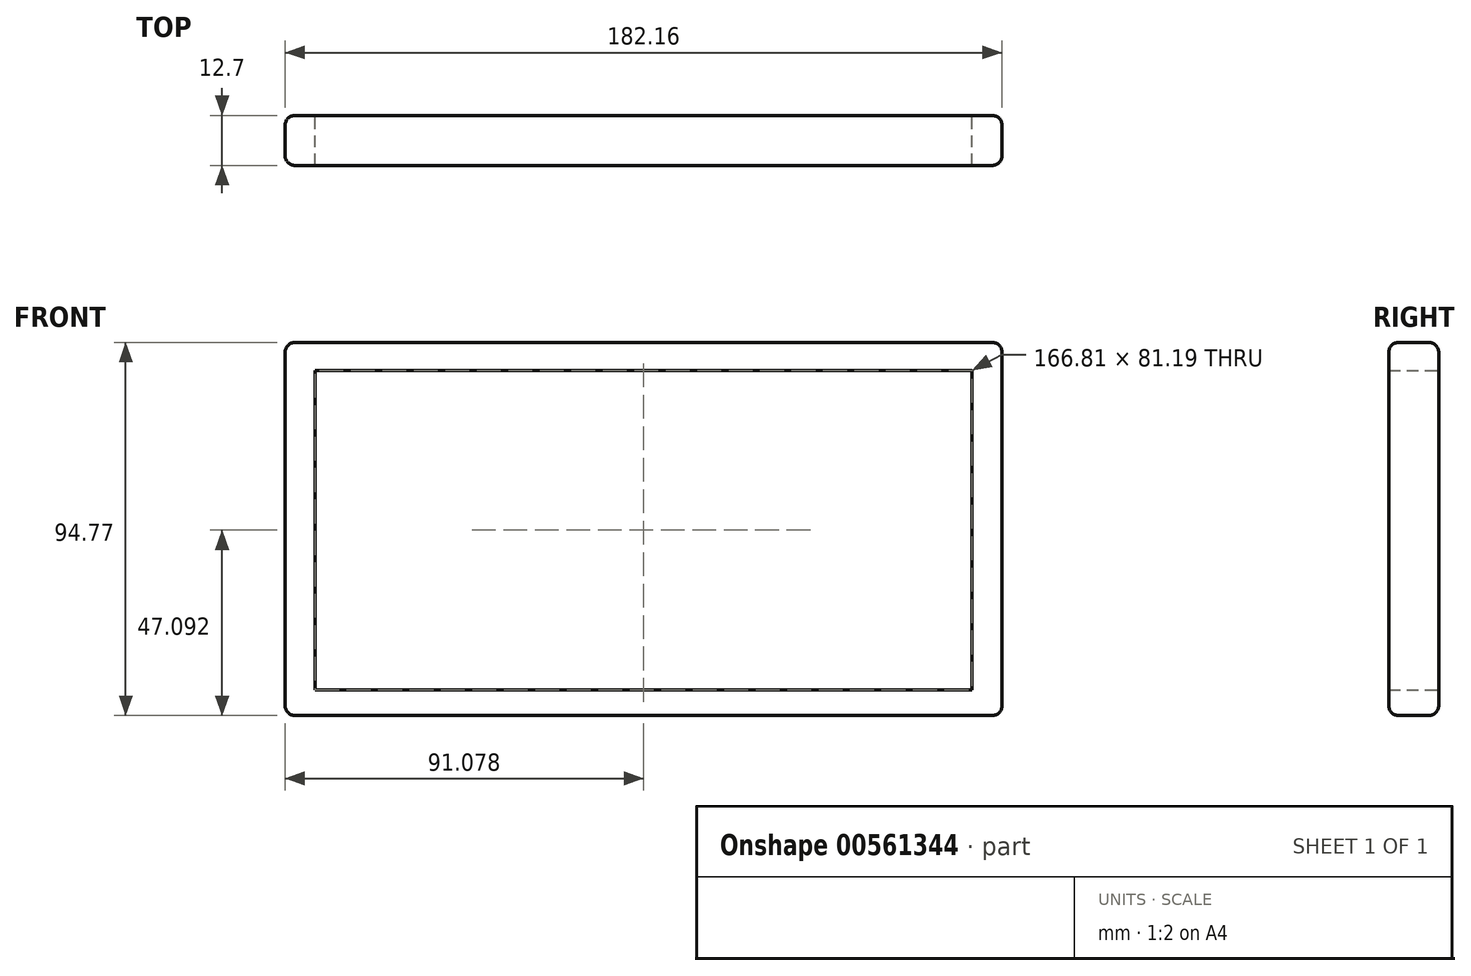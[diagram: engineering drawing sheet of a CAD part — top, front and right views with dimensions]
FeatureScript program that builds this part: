
annotation { "Feature Type Name" : "Feature", "Feature Type Description" : "" }
export const myFeature = defineFeature(function(context is Context, id is Id, definition is map)
    precondition{}
    {
        {
            var Q0;
            Q0=qCreatedBy(makeId("Front.planeOp"),FACE);
            var sketch = newSketch(context, id + "F0", { "sketchPlane" : qUnion([Q0])});
            skLineSegment(sketch, "E0.bottom", {"start": v(-92.1, 46.94) * mm, "end": v(90.07, 46.94) * mm});
            skLineSegment(sketch, "E0.top", {"start": v(-92.1, -47.83) * mm, "end": v(90.07, -47.83) * mm});
            skLineSegment(sketch, "E0.left", {"start": v(-92.1, 46.94) * mm, "end": v(-92.1, -47.83) * mm});
            skLineSegment(sketch, "E0.right", {"start": v(90.07, 46.94) * mm, "end": v(90.07, -47.83) * mm});
            skLineSegment(sketch, "E1.bottom", {"start": v(-84.42, 39.86) * mm, "end": v(82.4, 39.86) * mm});
            skLineSegment(sketch, "E1.top", {"start": v(-84.42, -41.33) * mm, "end": v(82.4, -41.33) * mm});
            skLineSegment(sketch, "E1.left", {"start": v(-84.42, 39.86) * mm, "end": v(-84.42, -41.33) * mm});
            skLineSegment(sketch, "E1.right", {"start": v(82.4, 39.86) * mm, "end": v(82.4, -41.33) * mm});
            skSolve(sketch);
        }
        {
            var Q0;
            Q0=makeQuery(id+"F0.imprint","IMPRINT",FACE,{"disambiguationData":[TD([[makeQuery(id+"F0.imprint","IMPRINT",EDGE,{"derivedFrom":sQuery(id+"F0.wireOp",EDGE,"E0.bottom")}),-1.0]])]});
            extrude(context, id + "F1", {"entities" : qUnion([Q0]), "depth" : 12.7 * mm, "offsetDistance" : 25.4 * mm});
        }
        {
            var Q0;
            Q0=makeQuery(id+"F1.opExtrude","CAP_EDGE",EDGE,{"disambiguationData":[OSD([sQuery(id+"F0.wireOp",EDGE,"E0.left")])],"isStart":false});
            var Q1;
            Q1=makeQuery(id+"F1.opExtrude","CAP_EDGE",EDGE,{"disambiguationData":[OSD([sQuery(id+"F0.wireOp",EDGE,"E0.bottom")])],"isStart":false});
            var Q2;
            Q2=makeQuery(id+"F1.opExtrude","CAP_EDGE",EDGE,{"disambiguationData":[OSD([sQuery(id+"F0.wireOp",EDGE,"E0.top")])],"isStart":false});
            var Q3;
            Q3=makeQuery(id+"F1.opExtrude","CAP_EDGE",EDGE,{"disambiguationData":[OSD([sQuery(id+"F0.wireOp",EDGE,"E0.right")])],"isStart":false});
            var Q4;
            Q4=makeQuery(id+"F1.opExtrude","SWEPT_EDGE",EDGE,{"disambiguationData":[OSD([sQuery(id+"F0.wireOp",EDGE,"E0.bottom"),sQuery(id+"F0.wireOp",EDGE,"E0.left")])]});
            var Q5;
            Q5=makeQuery(id+"F1.opExtrude","SWEPT_EDGE",EDGE,{"disambiguationData":[OSD([sQuery(id+"F0.wireOp",EDGE,"E0.top"),sQuery(id+"F0.wireOp",EDGE,"E0.left")])]});
            var Q6;
            Q6=makeQuery(id+"F1.opExtrude","SWEPT_EDGE",EDGE,{"disambiguationData":[OSD([sQuery(id+"F0.wireOp",EDGE,"E0.bottom"),sQuery(id+"F0.wireOp",EDGE,"E0.right")])]});
            var Q7;
            Q7=makeQuery(id+"F1.opExtrude","CAP_EDGE",EDGE,{"disambiguationData":[OSD([sQuery(id+"F0.wireOp",EDGE,"E0.right")])],"isStart":true});
            var Q8;
            Q8=makeQuery(id+"F1.opExtrude","SWEPT_EDGE",EDGE,{"disambiguationData":[OSD([sQuery(id+"F0.wireOp",EDGE,"E0.top"),sQuery(id+"F0.wireOp",EDGE,"E0.right")])]});
            var Q9;
            Q9=makeQuery(id+"F1.opExtrude","CAP_EDGE",EDGE,{"disambiguationData":[OSD([sQuery(id+"F0.wireOp",EDGE,"E0.top")])],"isStart":true});
            var Q10;
            Q10=makeQuery(id+"F1.opExtrude","CAP_EDGE",EDGE,{"disambiguationData":[OSD([sQuery(id+"F0.wireOp",EDGE,"E0.bottom")])],"isStart":true});
            var Q11;
            Q11=makeQuery(id+"F1.opExtrude","CAP_EDGE",EDGE,{"disambiguationData":[OSD([sQuery(id+"F0.wireOp",EDGE,"E0.left")])],"isStart":true});
            fillet(context, id + "F2", {"entities" : qUnion([Q0, Q1, Q2, Q3, Q4, Q5, Q6, Q7, Q8, Q9, Q10, Q11]), "radius" : 2.54 * mm, "allowEdgeOverflow" : false});
        }
    });
